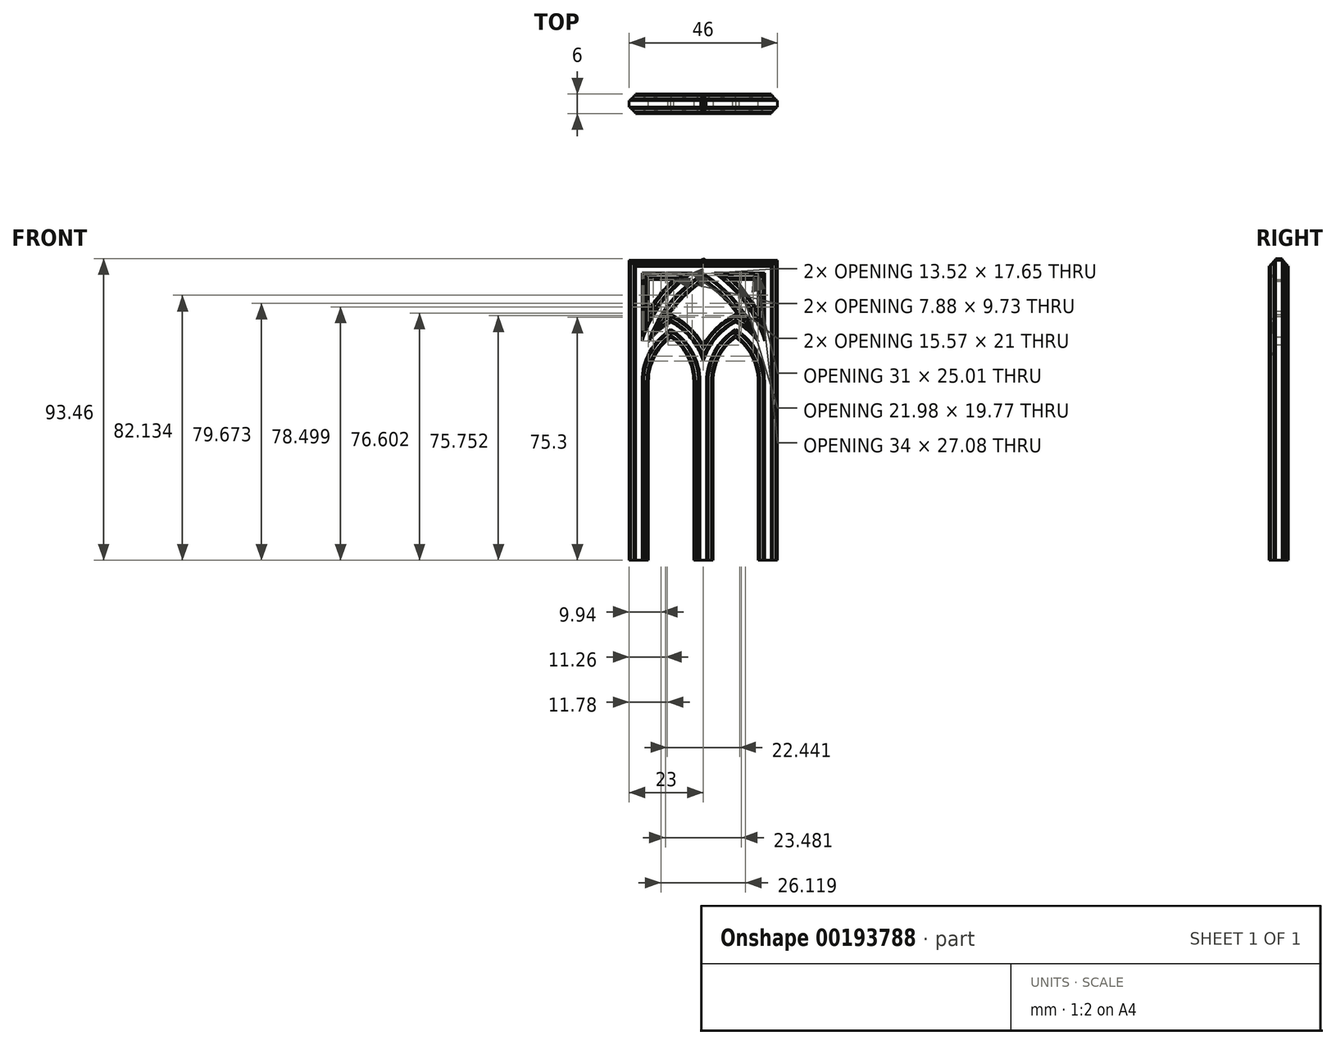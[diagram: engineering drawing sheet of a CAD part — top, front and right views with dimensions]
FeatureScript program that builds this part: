
annotation { "Feature Type Name" : "Feature", "Feature Type Description" : "" }
export const myFeature = defineFeature(function(context is Context, id is Id, definition is map)
    precondition{}
    {
        {
            var Q0;
            Q0=qCreatedBy(makeId("Front.planeOp"),FACE);
            var sketch = newSketch(context, id + "F0", { "sketchPlane" : qUnion([Q0])});
            skLineSegment(sketch, "E0", {"start": v(0, 0) * mm, "end": v(-20, 0) * mm, "construction": true});
            skLineSegment(sketch, "E1", {"start": v(0, 0) * mm, "end": v(20, 0) * mm, "construction": true});
            skLineSegment(sketch, "E2", {"start": v(-20, 0) * mm, "end": v(-20, 55.36) * mm});
            skLineSegment(sketch, "E3", {"start": v(-20, 90) * mm, "end": v(20, 90) * mm});
            skLineSegment(sketch, "E4", {"start": v(20, 90) * mm, "end": v(20, 0) * mm});
            skCircle(sketch, "E5", {"center": v(0, 90) * mm, "radius": 40 * mm, "construction": true});
            skArc(sketch, "E6", {"start": v(-20, 55.36) * mm, "mid": v(-14.64, 75.36) * mm, "end": v(0, 90) * mm});
            skArc(sketch, "E7", {"start": v(0, 90) * mm, "mid": v(14.64, 75.36) * mm, "end": v(20, 55.36) * mm});
            skLineSegment(sketch, "E8", {"start": v(-20, 55.36) * mm, "end": v(20, 55.36) * mm, "construction": true});
            skLineSegment(sketch, "E9", {"start": v(0, 55.36) * mm, "end": v(0, 0) * mm});
            skCircle(sketch, "E10", {"center": v(0, 55.36) * mm, "radius": 20 * mm, "construction": true});
            skCircle(sketch, "E11", {"center": v(-20, 55.36) * mm, "radius": 20 * mm, "construction": true});
            skCircle(sketch, "E12", {"center": v(20, 55.36) * mm, "radius": 20 * mm, "construction": true});
            skArc(sketch, "E13", {"start": v(-10, 72.68) * mm, "mid": v(-8.27, 71.56) * mm, "end": v(-6.67, 70.27) * mm});
            skArc(sketch, "E14", {"start": v(10, 72.68) * mm, "mid": v(2.68, 65.36) * mm, "end": v(0, 55.36) * mm});
            skArc(sketch, "E15", {"start": v(-10, 72.68) * mm, "mid": v(-11.81, 71.5) * mm, "end": v(-13.49, 70.13) * mm});
            skArc(sketch, "E16", {"start": v(10, 72.68) * mm, "mid": v(17.32, 65.36) * mm, "end": v(20, 55.36) * mm});
            skCircle(sketch, "E17", {"center": v(0, 77.72) * mm, "radius": 10 * mm});
            skPoint(sketch, "E17.first.point", {"position": v(-6.67, 85.17) * mm});
            skPoint(sketch, "E17.second.point", {"position": v(-6.67, 70.27) * mm});
            skPoint(sketch, "E17.third.point", {"position": v(6.67, 70.27) * mm});
            skPoint(sketch, "E18", {"position": v(6.67, 85.17) * mm});
            skArc(sketch, "E19", {"start": v(-20, 55.36) * mm, "mid": v(-10, 52.68) * mm, "end": v(0, 55.36) * mm, "construction": true});
            skArc(sketch, "E20", {"start": v(0, 55.36) * mm, "mid": v(10, 52.68) * mm, "end": v(20, 55.36) * mm, "construction": true});
            skLineSegment(sketch, "E21", {"start": v(-17.32, 65.36) * mm, "end": v(-10, 61.13) * mm, "construction": true});
            skLineSegment(sketch, "E22", {"start": v(-2.68, 65.36) * mm, "end": v(-10, 61.13) * mm, "construction": true});
            skLineSegment(sketch, "E23", {"start": v(0, 55.36) * mm, "end": v(10, 61.13) * mm, "construction": true});
            skLineSegment(sketch, "E24", {"start": v(20, 55.36) * mm, "end": v(10, 61.13) * mm, "construction": true});
            skPoint(sketch, "E25", {"position": v(-10, 61.13) * mm});
            skPoint(sketch, "E26", {"position": v(10, 61.13) * mm});
            skLineSegment(sketch, "E27", {"start": v(-10, 61.13) * mm, "end": v(-20, 55.36) * mm, "construction": true});
            skLineSegment(sketch, "E28", {"start": v(10, 61.13) * mm, "end": v(2.68, 65.36) * mm, "construction": true});
            skLineSegment(sketch, "E29", {"start": v(-10, 61.13) * mm, "end": v(0, 55.36) * mm, "construction": true});
            skLineSegment(sketch, "E30", {"start": v(10, 61.13) * mm, "end": v(17.32, 65.36) * mm, "construction": true});
            skLineSegment(sketch, "E31", {"start": v(-10, 61.13) * mm, "end": v(-10, 72.68) * mm, "construction": true});
            skLineSegment(sketch, "E32", {"start": v(10, 61.13) * mm, "end": v(10, 72.68) * mm, "construction": true});
            skPoint(sketch, "E33.second.point", {"position": v(-16.04, 53.61) * mm});
            skPoint(sketch, "E34.first.point", {"position": v(-13.49, 70.13) * mm});
            skPoint(sketch, "E34.second.point", {"position": v(-6.51, 70.13) * mm});
            skPoint(sketch, "E35", {"position": v(-14.48, 63.72) * mm});
            skPoint(sketch, "E36.first.point", {"position": v(-0.47, 59.66) * mm});
            skPoint(sketch, "E36.second.point", {"position": v(-3.96, 53.61) * mm});
            skArc(sketch, "E37", {"start": v(-14.48, 63.72) * mm, "mid": v(-10, 61.13) * mm, "end": v(-5.52, 63.72) * mm, "construction": true});
            skArc(sketch, "E38", {"start": v(-13.49, 70.13) * mm, "mid": v(-15.11, 67.1) * mm, "end": v(-14.48, 63.72) * mm});
            skArc(sketch, "E39", {"start": v(-19.53, 59.66) * mm, "mid": v(-11.24, 54.51) * mm, "end": v(-14.48, 63.72) * mm, "construction": true});
            skArc(sketch, "E40", {"start": v(-14.48, 63.72) * mm, "mid": v(-17.72, 62.58) * mm, "end": v(-19.53, 59.66) * mm});
            skArc(sketch, "E41", {"start": v(-5.52, 63.72) * mm, "mid": v(-4.89, 67.1) * mm, "end": v(-6.51, 70.13) * mm});
            skArc(sketch, "E42", {"start": v(-6.51, 70.13) * mm, "mid": v(-10, 71.48) * mm, "end": v(-13.49, 70.13) * mm, "construction": true});
            skLineSegment(sketch, "E43", {"start": v(-5.52, 63.72) * mm, "end": v(-5.52, 63.72) * mm});
            skArc(sketch, "E44", {"start": v(-5.52, 63.72) * mm, "mid": v(-8.76, 54.51) * mm, "end": v(-0.47, 59.66) * mm, "construction": true});
            skArc(sketch, "E45", {"start": v(-0.47, 59.66) * mm, "mid": v(-2.28, 62.58) * mm, "end": v(-5.52, 63.72) * mm});
            skArc(sketch, "E46", {"start": v(-13.49, 70.13) * mm, "mid": v(-17.32, 65.36) * mm, "end": v(-19.53, 59.66) * mm});
            skArc(sketch, "E47", {"start": v(-19.53, 59.66) * mm, "mid": v(-19.88, 57.52) * mm, "end": v(-20, 55.36) * mm});
            skArc(sketch, "E48", {"start": v(-6.51, 70.13) * mm, "mid": v(-2.68, 65.36) * mm, "end": v(-0.47, 59.66) * mm});
            skArc(sketch, "E49", {"start": v(-6.67, 70.27) * mm, "mid": v(-6.59, 70.2) * mm, "end": v(-6.51, 70.13) * mm});
            skArc(sketch, "E50", {"start": v(-0.47, 59.66) * mm, "mid": v(-0.12, 57.52) * mm, "end": v(0, 55.36) * mm});
            skLineSegment(sketch, "E51", {"start": v(0, 77.72) * mm, "end": v(7.07, 84.8) * mm, "construction": true});
            skLineSegment(sketch, "E52", {"start": v(-7.07, 84.8) * mm, "end": v(0, 77.72) * mm, "construction": true});
            skLineSegment(sketch, "E53", {"start": v(0, 77.72) * mm, "end": v(-7.07, 70.65) * mm, "construction": true});
            skLineSegment(sketch, "E54", {"start": v(0, 77.72) * mm, "end": v(7.07, 70.65) * mm, "construction": true});
            skArc(sketch, "E55", {"start": v(-7.07, 84.8) * mm, "mid": v(-8.54, 81.26) * mm, "end": v(-7.07, 77.72) * mm});
            skArc(sketch, "E56", {"start": v(-7.07, 77.72) * mm, "mid": v(0, 77.72) * mm, "end": v(0, 84.8) * mm, "construction": true});
            skArc(sketch, "E57", {"start": v(-7.07, 77.72) * mm, "mid": v(-8.54, 74.18) * mm, "end": v(-7.07, 70.65) * mm});
            skArc(sketch, "E58", {"start": v(-7.07, 70.65) * mm, "mid": v(-3.54, 69.18) * mm, "end": v(0, 70.65) * mm});
            skArc(sketch, "E59", {"start": v(0, 70.65) * mm, "mid": v(0, 77.72) * mm, "end": v(-7.07, 77.72) * mm, "construction": true});
            skArc(sketch, "E60", {"start": v(0, 70.65) * mm, "mid": v(3.54, 69.18) * mm, "end": v(7.07, 70.65) * mm});
            skArc(sketch, "E61", {"start": v(7.07, 70.65) * mm, "mid": v(8.54, 74.18) * mm, "end": v(7.07, 77.72) * mm});
            skLineSegment(sketch, "E62", {"start": v(7.07, 70.65) * mm, "end": v(7.07, 70.65) * mm});
            skArc(sketch, "E63", {"start": v(7.07, 77.72) * mm, "mid": v(0, 77.72) * mm, "end": v(0, 70.65) * mm, "construction": true});
            skArc(sketch, "E64", {"start": v(7.07, 77.72) * mm, "mid": v(8.54, 81.26) * mm, "end": v(7.07, 84.8) * mm});
            skArc(sketch, "E65", {"start": v(7.07, 84.8) * mm, "mid": v(3.54, 86.26) * mm, "end": v(0, 84.8) * mm});
            skLineSegment(sketch, "E66", {"start": v(0, 84.8) * mm, "end": v(0, 84.8) * mm});
            skArc(sketch, "E67", {"start": v(0, 84.8) * mm, "mid": v(0, 77.72) * mm, "end": v(7.07, 77.72) * mm, "construction": true});
            skArc(sketch, "E68", {"start": v(0, 84.8) * mm, "mid": v(-3.54, 86.26) * mm, "end": v(-7.07, 84.8) * mm});
            skLineSegment(sketch, "E69", {"start": v(0, 90) * mm, "end": v(-20, 55.36) * mm, "construction": true});
            skLineSegment(sketch, "E70", {"start": v(-20, 90) * mm, "end": v(-20, 55.36) * mm, "construction": true});
            skLineSegment(sketch, "E71", {"start": v(-20, 55.36) * mm, "end": v(-20, 90) * mm});
            skCircle(sketch, "E72", {"center": v(14.64, 84.64) * mm, "radius": 5.36 * mm, "construction": true});
            skPoint(sketch, "E72.first.point", {"position": v(14.64, 90) * mm});
            skPoint(sketch, "E72.second.point", {"position": v(20, 84.64) * mm});
            skPoint(sketch, "E72.third.point", {"position": v(10.55, 81.18) * mm});
            skPoint(sketch, "E73.first.point", {"position": v(16.86, 90) * mm});
            skPoint(sketch, "E73.second.point", {"position": v(20, 86.86) * mm});
            skPoint(sketch, "E74.second.point", {"position": v(12.65, 78.47) * mm});
            skPoint(sketch, "E74.third.point", {"position": v(20, 80.81) * mm});
            skPoint(sketch, "E75.second.point", {"position": v(8.43, 83.5) * mm});
            skPoint(sketch, "E75.third.point", {"position": v(11.15, 90) * mm});
            skCircle(sketch, "E76", {"center": v(-14.64, 84.64) * mm, "radius": 5.36 * mm, "construction": true});
            skPoint(sketch, "E76.first.point", {"position": v(-14.64, 90) * mm});
            skPoint(sketch, "E76.second.point", {"position": v(-20, 84.64) * mm});
            skPoint(sketch, "E76.third.point", {"position": v(-10.55, 81.18) * mm});
            skPoint(sketch, "E77.first.point", {"position": v(-16.86, 90) * mm});
            skPoint(sketch, "E77.second.point", {"position": v(-20, 86.86) * mm});
            skPoint(sketch, "E78.first.point", {"position": v(-11.15, 90) * mm});
            skPoint(sketch, "E78.second.point", {"position": v(-8.43, 83.5) * mm});
            skPoint(sketch, "E79.second.point", {"position": v(-20, 80.81) * mm});
            skPoint(sketch, "E79.third.point", {"position": v(-12.65, 78.47) * mm});
            skArc(sketch, "E80", {"start": v(-18.33, 84.09) * mm, "mid": v(-14.57, 84.71) * mm, "end": v(-14.18, 88.5) * mm, "construction": true});
            skArc(sketch, "E81", {"start": v(-20, 86.86) * mm, "mid": v(-19.55, 85.24) * mm, "end": v(-18.33, 84.09) * mm});
            skArc(sketch, "E82", {"start": v(-16.86, 90) * mm, "mid": v(-19.08, 89.08) * mm, "end": v(-20, 86.86) * mm, "construction": true});
            skArc(sketch, "E83", {"start": v(-14.18, 88.5) * mm, "mid": v(-15.33, 89.6) * mm, "end": v(-16.86, 90) * mm});
            skArc(sketch, "E84", {"start": v(-14.18, 88.5) * mm, "mid": v(-14.79, 85.03) * mm, "end": v(-12.29, 82.54) * mm, "construction": true});
            skArc(sketch, "E85", {"start": v(-11.15, 90) * mm, "mid": v(-12.84, 89.6) * mm, "end": v(-14.18, 88.5) * mm});
            skArc(sketch, "E86", {"start": v(-8.43, 83.5) * mm, "mid": v(-7.62, 87.65) * mm, "end": v(-11.15, 90) * mm, "construction": true});
            skArc(sketch, "E87", {"start": v(-12.29, 82.54) * mm, "mid": v(-10.23, 82.47) * mm, "end": v(-8.43, 83.5) * mm});
            skArc(sketch, "E88", {"start": v(-12.29, 82.54) * mm, "mid": v(-14.95, 84.73) * mm, "end": v(-18.33, 84.09) * mm, "construction": true});
            skArc(sketch, "E89", {"start": v(-12.65, 78.47) * mm, "mid": v(-11.92, 80.46) * mm, "end": v(-12.29, 82.54) * mm});
            skArc(sketch, "E90", {"start": v(-20, 80.81) * mm, "mid": v(-17.18, 76.95) * mm, "end": v(-12.65, 78.47) * mm, "construction": true});
            skArc(sketch, "E91", {"start": v(-18.33, 84.09) * mm, "mid": v(-19.56, 82.65) * mm, "end": v(-20, 80.81) * mm});
            skArc(sketch, "E92", {"start": v(12.29, 82.54) * mm, "mid": v(14.79, 85.03) * mm, "end": v(14.18, 88.5) * mm, "construction": true});
            skArc(sketch, "E93", {"start": v(8.43, 83.5) * mm, "mid": v(10.23, 82.47) * mm, "end": v(12.29, 82.54) * mm});
            skArc(sketch, "E94", {"start": v(12.29, 82.54) * mm, "mid": v(11.92, 80.46) * mm, "end": v(12.65, 78.47) * mm});
            skArc(sketch, "E95", {"start": v(12.65, 78.47) * mm, "mid": v(17.18, 76.95) * mm, "end": v(20, 80.81) * mm, "construction": true});
            skArc(sketch, "E96", {"start": v(20, 80.81) * mm, "mid": v(19.56, 82.65) * mm, "end": v(18.33, 84.09) * mm});
            skArc(sketch, "E97", {"start": v(18.33, 84.09) * mm, "mid": v(19.55, 85.24) * mm, "end": v(20, 86.86) * mm});
            skArc(sketch, "E98", {"start": v(20, 86.86) * mm, "mid": v(19.08, 89.08) * mm, "end": v(16.86, 90) * mm, "construction": true});
            skArc(sketch, "E99", {"start": v(18.33, 84.09) * mm, "mid": v(14.95, 84.73) * mm, "end": v(12.29, 82.54) * mm, "construction": true});
            skArc(sketch, "E100", {"start": v(14.18, 88.5) * mm, "mid": v(14.57, 84.71) * mm, "end": v(18.33, 84.09) * mm, "construction": true});
            skArc(sketch, "E101", {"start": v(16.86, 90) * mm, "mid": v(15.33, 89.6) * mm, "end": v(14.18, 88.5) * mm});
            skArc(sketch, "E102", {"start": v(11.15, 90) * mm, "mid": v(7.62, 87.65) * mm, "end": v(8.43, 83.5) * mm, "construction": true});
            skArc(sketch, "E103", {"start": v(14.18, 88.5) * mm, "mid": v(12.84, 89.6) * mm, "end": v(11.15, 90) * mm});
            skSolve(sketch);
        }
        {
            var Q0;
            Q0=qCreatedBy(makeId("Top.planeOp"),FACE);
            var sketch = newSketch(context, id + "F1", { "sketchPlane" : qUnion([Q0])});
            skPoint(sketch, "E104.0", {"position": v(-20, 0) * mm});
            skPoint(sketch, "E104.1", {"position": v(0, 0) * mm});
            skPoint(sketch, "E104.2", {"position": v(20, 0) * mm});
            skLineSegment(sketch, "E105.bottom", {"start": v(-17, 1) * mm, "end": v(-17.5, 1) * mm});
            skLineSegment(sketch, "E105.top", {"start": v(-17, -1) * mm, "end": v(-17.5, -1) * mm});
            skLineSegment(sketch, "E105.left", {"start": v(-17, 1) * mm, "end": v(-17, -1) * mm});
            skLineSegment(sketch, "E105.right", {"start": v(-23, 1) * mm, "end": v(-23, -1) * mm});
            skLineSegment(sketch, "E106.bottom", {"start": v(-21, 3) * mm, "end": v(-19, 3) * mm});
            skLineSegment(sketch, "E106.top", {"start": v(-21, -3) * mm, "end": v(-19, -3) * mm});
            skLineSegment(sketch, "E106.left", {"start": v(-21, 3) * mm, "end": v(-21, 2.5) * mm});
            skLineSegment(sketch, "E106.right", {"start": v(-19, 3) * mm, "end": v(-19, 2.5) * mm});
            skLineSegment(sketch, "E107", {"start": v(-21, 2.5) * mm, "end": v(-21.5, 2.5) * mm});
            skLineSegment(sketch, "E108", {"start": v(-21.5, 2.5) * mm, "end": v(-22.5, 1.5) * mm, "construction": true});
            skLineSegment(sketch, "E109", {"start": v(-22.5, 1.5) * mm, "end": v(-22.5, 1) * mm});
            skLineSegment(sketch, "E110", {"start": v(-22.5, 1) * mm, "end": v(-22.5, -1) * mm, "construction": true});
            skLineSegment(sketch, "E111", {"start": v(-22.5, -1) * mm, "end": v(-22.5, -1.5) * mm});
            skLineSegment(sketch, "E112", {"start": v(-22.5, -1.5) * mm, "end": v(-21.5, -2.5) * mm, "construction": true});
            skLineSegment(sketch, "E113", {"start": v(-21.5, -2.5) * mm, "end": v(-21, -2.5) * mm});
            skLineSegment(sketch, "E114", {"start": v(-21, -2.5) * mm, "end": v(-19, -2.5) * mm});
            skLineSegment(sketch, "E115", {"start": v(-19, -2.5) * mm, "end": v(-18.5, -2.5) * mm});
            skLineSegment(sketch, "E116", {"start": v(-18.5, -2.5) * mm, "end": v(-17.5, -1.5) * mm, "construction": true});
            skLineSegment(sketch, "E117", {"start": v(-17.5, -1.5) * mm, "end": v(-17.5, -1) * mm});
            skLineSegment(sketch, "E118", {"start": v(-17.5, -1) * mm, "end": v(-17.5, 1) * mm, "construction": true});
            skLineSegment(sketch, "E119", {"start": v(-17.5, 1) * mm, "end": v(-17.5, 1.5) * mm});
            skLineSegment(sketch, "E120", {"start": v(-17.5, 1.5) * mm, "end": v(-18.5, 2.5) * mm, "construction": true});
            skLineSegment(sketch, "E121", {"start": v(-18.5, 2.5) * mm, "end": v(-19, 2.5) * mm});
            skLineSegment(sketch, "E122", {"start": v(-19, 2.5) * mm, "end": v(-21, 2.5) * mm});
            skLineSegment(sketch, "E123", {"start": v(-23, 1) * mm, "end": v(-23, 3) * mm, "construction": true});
            skLineSegment(sketch, "E124", {"start": v(-23, 3) * mm, "end": v(-21, 3) * mm, "construction": true});
            skLineSegment(sketch, "E125", {"start": v(-19, 3) * mm, "end": v(-17, 3) * mm, "construction": true});
            skLineSegment(sketch, "E126", {"start": v(-17, 3) * mm, "end": v(-17, 1) * mm, "construction": true});
            skLineSegment(sketch, "E127", {"start": v(-17, -1) * mm, "end": v(-17, -3) * mm, "construction": true});
            skLineSegment(sketch, "E128", {"start": v(-17, -3) * mm, "end": v(-19, -3) * mm, "construction": true});
            skLineSegment(sketch, "E129", {"start": v(-21, -3) * mm, "end": v(-23, -3) * mm, "construction": true});
            skLineSegment(sketch, "E130", {"start": v(-23, -3) * mm, "end": v(-23, -1) * mm, "construction": true});
            skArc(sketch, "E131", {"start": v(-22.5, 1.5) * mm, "mid": v(-21.88, 1.88) * mm, "end": v(-21.5, 2.5) * mm});
            skArc(sketch, "E132", {"start": v(-18.5, 2.5) * mm, "mid": v(-18.12, 1.88) * mm, "end": v(-17.5, 1.5) * mm});
            skArc(sketch, "E133", {"start": v(-21.5, -2.5) * mm, "mid": v(-21.88, -1.88) * mm, "end": v(-22.5, -1.5) * mm});
            skArc(sketch, "E134", {"start": v(-17.5, -1.5) * mm, "mid": v(-18.12, -1.88) * mm, "end": v(-18.5, -2.5) * mm});
            skLineSegment(sketch, "E135", {"start": v(-21, 2.5) * mm, "end": v(-21, -2.5) * mm, "construction": true});
            skLineSegment(sketch, "E136", {"start": v(-19, 2.5) * mm, "end": v(-19, -2.5) * mm, "construction": true});
            skLineSegment(sketch, "E137", {"start": v(-17.5, 1) * mm, "end": v(-22.5, 1) * mm, "construction": true});
            skLineSegment(sketch, "E138", {"start": v(-17.5, -1) * mm, "end": v(-22.5, -1) * mm, "construction": true});
            skLineSegment(sketch, "E139", {"start": v(-19, -2.5) * mm, "end": v(-19, -3) * mm});
            skLineSegment(sketch, "E140", {"start": v(-21, -2.5) * mm, "end": v(-21, -3) * mm});
            skLineSegment(sketch, "E141", {"start": v(-22.5, -1) * mm, "end": v(-23, -1) * mm});
            skLineSegment(sketch, "E142", {"start": v(-22.5, 1) * mm, "end": v(-23, 1) * mm});
            skLineSegment(sketch, "E143.1.0.1", {"start": v(-1, -3) * mm, "end": v(1, -3) * mm});
            skLineSegment(sketch, "E143.1.0.2", {"start": v(1, -2.5) * mm, "end": v(1, -3) * mm});
            skLineSegment(sketch, "E143.1.0.3", {"start": v(1, -2.5) * mm, "end": v(1.5, -2.5) * mm});
            skArc(sketch, "E143.1.0.4", {"start": v(2.5, -1.5) * mm, "mid": v(1.88, -1.88) * mm, "end": v(1.5, -2.5) * mm});
            skLineSegment(sketch, "E143.1.0.5", {"start": v(2.5, -1.5) * mm, "end": v(2.5, -1) * mm});
            skLineSegment(sketch, "E143.1.0.6", {"start": v(3, -1) * mm, "end": v(2.5, -1) * mm});
            skLineSegment(sketch, "E143.1.0.7", {"start": v(3, 1) * mm, "end": v(3, -1) * mm});
            skLineSegment(sketch, "E143.1.0.8", {"start": v(-1, -2.5) * mm, "end": v(-1, -3) * mm});
            skLineSegment(sketch, "E143.1.0.9", {"start": v(-1.5, -2.5) * mm, "end": v(-1, -2.5) * mm});
            skArc(sketch, "E143.1.0.10", {"start": v(-1.5, -2.5) * mm, "mid": v(-1.88, -1.88) * mm, "end": v(-2.5, -1.5) * mm});
            skLineSegment(sketch, "E143.1.0.11", {"start": v(-2.5, -1) * mm, "end": v(-2.5, -1.5) * mm});
            skLineSegment(sketch, "E143.1.0.12", {"start": v(-2.5, -1) * mm, "end": v(-3, -1) * mm});
            skLineSegment(sketch, "E143.1.0.13", {"start": v(-3, 1) * mm, "end": v(-3, -1) * mm});
            skLineSegment(sketch, "E143.1.0.14", {"start": v(-2.5, 1) * mm, "end": v(-3, 1) * mm});
            skLineSegment(sketch, "E143.1.0.15", {"start": v(-2.5, 1.5) * mm, "end": v(-2.5, 1) * mm});
            skArc(sketch, "E143.1.0.16", {"start": v(-2.5, 1.5) * mm, "mid": v(-1.88, 1.88) * mm, "end": v(-1.5, 2.5) * mm});
            skLineSegment(sketch, "E143.1.0.17", {"start": v(-1, 2.5) * mm, "end": v(-1.5, 2.5) * mm});
            skLineSegment(sketch, "E143.1.0.18", {"start": v(-1, 3) * mm, "end": v(-1, 2.5) * mm});
            skLineSegment(sketch, "E143.1.0.19", {"start": v(-1, 3) * mm, "end": v(1, 3) * mm});
            skLineSegment(sketch, "E143.1.0.20", {"start": v(1, 3) * mm, "end": v(1, 2.5) * mm});
            skLineSegment(sketch, "E143.1.0.21", {"start": v(1.5, 2.5) * mm, "end": v(1, 2.5) * mm});
            skArc(sketch, "E143.1.0.22", {"start": v(1.5, 2.5) * mm, "mid": v(1.88, 1.88) * mm, "end": v(2.5, 1.5) * mm});
            skLineSegment(sketch, "E143.1.0.23", {"start": v(2.5, 1) * mm, "end": v(2.5, 1.5) * mm});
            skLineSegment(sketch, "E143.1.0.24", {"start": v(3, 1) * mm, "end": v(2.5, 1) * mm});
            skLineSegment(sketch, "E143.2.0.1", {"start": v(19, -3) * mm, "end": v(21, -3) * mm});
            skLineSegment(sketch, "E143.2.0.2", {"start": v(21, -2.5) * mm, "end": v(21, -3) * mm});
            skLineSegment(sketch, "E143.2.0.3", {"start": v(21, -2.5) * mm, "end": v(21.5, -2.5) * mm});
            skArc(sketch, "E143.2.0.4", {"start": v(22.5, -1.5) * mm, "mid": v(21.88, -1.88) * mm, "end": v(21.5, -2.5) * mm});
            skLineSegment(sketch, "E143.2.0.5", {"start": v(22.5, -1.5) * mm, "end": v(22.5, -1) * mm});
            skLineSegment(sketch, "E143.2.0.6", {"start": v(23, -1) * mm, "end": v(22.5, -1) * mm});
            skLineSegment(sketch, "E143.2.0.7", {"start": v(23, 1) * mm, "end": v(23, -1) * mm});
            skLineSegment(sketch, "E143.2.0.8", {"start": v(19, -2.5) * mm, "end": v(19, -3) * mm});
            skLineSegment(sketch, "E143.2.0.9", {"start": v(18.5, -2.5) * mm, "end": v(19, -2.5) * mm});
            skArc(sketch, "E143.2.0.10", {"start": v(18.5, -2.5) * mm, "mid": v(18.12, -1.88) * mm, "end": v(17.5, -1.5) * mm});
            skLineSegment(sketch, "E143.2.0.11", {"start": v(17.5, -1) * mm, "end": v(17.5, -1.5) * mm});
            skLineSegment(sketch, "E143.2.0.12", {"start": v(17.5, -1) * mm, "end": v(17, -1) * mm});
            skLineSegment(sketch, "E143.2.0.13", {"start": v(17, 1) * mm, "end": v(17, -1) * mm});
            skLineSegment(sketch, "E143.2.0.14", {"start": v(17.5, 1) * mm, "end": v(17, 1) * mm});
            skLineSegment(sketch, "E143.2.0.15", {"start": v(17.5, 1.5) * mm, "end": v(17.5, 1) * mm});
            skArc(sketch, "E143.2.0.16", {"start": v(17.5, 1.5) * mm, "mid": v(18.12, 1.88) * mm, "end": v(18.5, 2.5) * mm});
            skLineSegment(sketch, "E143.2.0.17", {"start": v(19, 2.5) * mm, "end": v(18.5, 2.5) * mm});
            skLineSegment(sketch, "E143.2.0.18", {"start": v(19, 3) * mm, "end": v(19, 2.5) * mm});
            skLineSegment(sketch, "E143.2.0.19", {"start": v(19, 3) * mm, "end": v(21, 3) * mm});
            skLineSegment(sketch, "E143.2.0.20", {"start": v(21, 3) * mm, "end": v(21, 2.5) * mm});
            skLineSegment(sketch, "E143.2.0.21", {"start": v(21.5, 2.5) * mm, "end": v(21, 2.5) * mm});
            skArc(sketch, "E143.2.0.22", {"start": v(21.5, 2.5) * mm, "mid": v(21.88, 1.88) * mm, "end": v(22.5, 1.5) * mm});
            skLineSegment(sketch, "E143.2.0.23", {"start": v(22.5, 1) * mm, "end": v(22.5, 1.5) * mm});
            skLineSegment(sketch, "E143.2.0.24", {"start": v(23, 1) * mm, "end": v(22.5, 1) * mm});
            skLineSegment(sketch, "E143.direction1", {"start": v(-20, 0) * mm, "end": v(0, 0) * mm, "construction": true});
            skLineSegment(sketch, "E144", {"start": v(-1, 2.5) * mm, "end": v(1, 2.5) * mm});
            skLineSegment(sketch, "E145", {"start": v(1, -2.5) * mm, "end": v(-1, -2.5) * mm});
            skLineSegment(sketch, "E146", {"start": v(19, 2.5) * mm, "end": v(21, 2.5) * mm});
            skLineSegment(sketch, "E147", {"start": v(21, -2.5) * mm, "end": v(19, -2.5) * mm});
            skSolve(sketch);
        }
        {
            var Q0;
            Q0=makeQuery(id+"F1.imprint","IMPRINT",FACE,{"disambiguationData":[TD([[makeQuery(id+"F1.imprint","IMPRINT",EDGE,{"derivedFrom":sQuery(id+"F1.wireOp",EDGE,"E105.bottom")}),1.0]])]});
            var Q1;
            Q1=makeQuery(id+"F1.imprint","IMPRINT",FACE,{"disambiguationData":[TD([[makeQuery(id+"F1.imprint","IMPRINT",EDGE,{"derivedFrom":sQuery(id+"F1.wireOp",EDGE,"E106.top")}),1.0]])]});
            var Q2;
            Q2=makeQuery(id+"F1.imprint","IMPRINT",FACE,{"disambiguationData":[TD([[makeQuery(id+"F1.imprint","IMPRINT",EDGE,{"derivedFrom":sQuery(id+"F1.wireOp",EDGE,"E106.bottom")}),-1.0]])]});
            var Q3;
            Q3=sQuery(id+"F0.wireOp",EDGE,"E2");
            var Q4;
            Q4=sQuery(id+"F0.wireOp",EDGE,"E6");
            var Q5;
            Q5=sQuery(id+"F0.wireOp",EDGE,"E7");
            sweep(context, id + "F2", {"profiles" : qUnion([Q0, Q1, Q2]), "path" : qUnion([Q3, Q4, Q5])});
        }
        {
            var Q0;
            Q0=makeQuery(id+"F1.imprint","IMPRINT",FACE,{"disambiguationData":[TD([[makeQuery(id+"F1.imprint","IMPRINT",EDGE,{"derivedFrom":sQuery(id+"F1.wireOp",EDGE,"E143.2.0.1")}),1.0]])]});
            var Q1;
            Q1=makeQuery(id+"F1.imprint","IMPRINT",FACE,{"disambiguationData":[TD([[makeQuery(id+"F1.imprint","IMPRINT",EDGE,{"derivedFrom":sQuery(id+"F1.wireOp",EDGE,"E143.2.0.3")}),1.0]])]});
            var Q2;
            Q2=makeQuery(id+"F1.imprint","IMPRINT",FACE,{"disambiguationData":[TD([[makeQuery(id+"F1.imprint","IMPRINT",EDGE,{"derivedFrom":sQuery(id+"F1.wireOp",EDGE,"E143.2.0.18")}),1.0]])]});
            var Q3;
            Q3=sQuery(id+"F0.wireOp",EDGE,"E4");
            var Q4;
            Q4=sQuery(id+"F0.wireOp",EDGE,"E3");
            var Q5;
            Q5=sQuery(id+"F0.wireOp",EDGE,"E71");
            sweep(context, id + "F3", {"operationType" : NewBodyOperationType.ADD, "profiles" : qUnion([Q0, Q1, Q2]), "path" : qUnion([Q3, Q4, Q5])});
        }
        {
            var Q0;
            Q0=makeQuery(id+"F1.imprint","IMPRINT",FACE,{"disambiguationData":[TD([[makeQuery(id+"F1.imprint","IMPRINT",EDGE,{"derivedFrom":sQuery(id+"F1.wireOp",EDGE,"E143.1.0.1")}),1.0]])]});
            var Q1;
            Q1=makeQuery(id+"F1.imprint","IMPRINT",FACE,{"disambiguationData":[TD([[makeQuery(id+"F1.imprint","IMPRINT",EDGE,{"derivedFrom":sQuery(id+"F1.wireOp",EDGE,"E143.1.0.3")}),1.0]])]});
            var Q2;
            Q2=makeQuery(id+"F1.imprint","IMPRINT",FACE,{"disambiguationData":[TD([[makeQuery(id+"F1.imprint","IMPRINT",EDGE,{"derivedFrom":sQuery(id+"F1.wireOp",EDGE,"E143.1.0.18")}),1.0]])]});
            var Q3;
            Q3=sQuery(id+"F0.wireOp",EDGE,"E9");
            var Q4;
            Q4=sQuery(id+"F0.wireOp",EDGE,"E48");
            var Q5;
            Q5=sQuery(id+"F0.wireOp",EDGE,"E50");
            var Q6;
            Q6=sQuery(id+"F0.wireOp",EDGE,"E13");
            var Q7;
            Q7=sQuery(id+"F0.wireOp",EDGE,"E49");
            var Q8;
            Q8=sQuery(id+"F0.wireOp",EDGE,"E15");
            var Q9;
            Q9=sQuery(id+"F0.wireOp",EDGE,"E46");
            var Q10;
            Q10=sQuery(id+"F0.wireOp",EDGE,"E47");
            sweep(context, id + "F4", {"operationType" : NewBodyOperationType.ADD, "profiles" : qUnion([Q0, Q1, Q2]), "path" : qUnion([Q3, Q4, Q5, Q6, Q7, Q8, Q9, Q10])});
        }
        {
            var Q0;
            Q0=makeQuery(id+"F1.imprint","IMPRINT",FACE,{"disambiguationData":[TD([[makeQuery(id+"F1.imprint","IMPRINT",EDGE,{"derivedFrom":sQuery(id+"F1.wireOp",EDGE,"E143.1.0.3")}),1.0]])]});
            var Q1;
            Q1=makeQuery(id+"F1.imprint","IMPRINT",FACE,{"disambiguationData":[TD([[makeQuery(id+"F1.imprint","IMPRINT",EDGE,{"derivedFrom":sQuery(id+"F1.wireOp",EDGE,"E143.1.0.1")}),1.0]])]});
            var Q2;
            Q2=makeQuery(id+"F1.imprint","IMPRINT",FACE,{"disambiguationData":[TD([[makeQuery(id+"F1.imprint","IMPRINT",EDGE,{"derivedFrom":sQuery(id+"F1.wireOp",EDGE,"E143.1.0.18")}),1.0]])]});
            var Q3;
            Q3=sQuery(id+"F0.wireOp",EDGE,"E9");
            var Q4;
            Q4=sQuery(id+"F0.wireOp",EDGE,"E14");
            var Q5;
            Q5=sQuery(id+"F0.wireOp",EDGE,"E16");
            sweep(context, id + "F5", {"operationType" : NewBodyOperationType.ADD, "profiles" : qUnion([Q0, Q1, Q2]), "path" : qUnion([Q3, Q4, Q5])});
        }
    });
